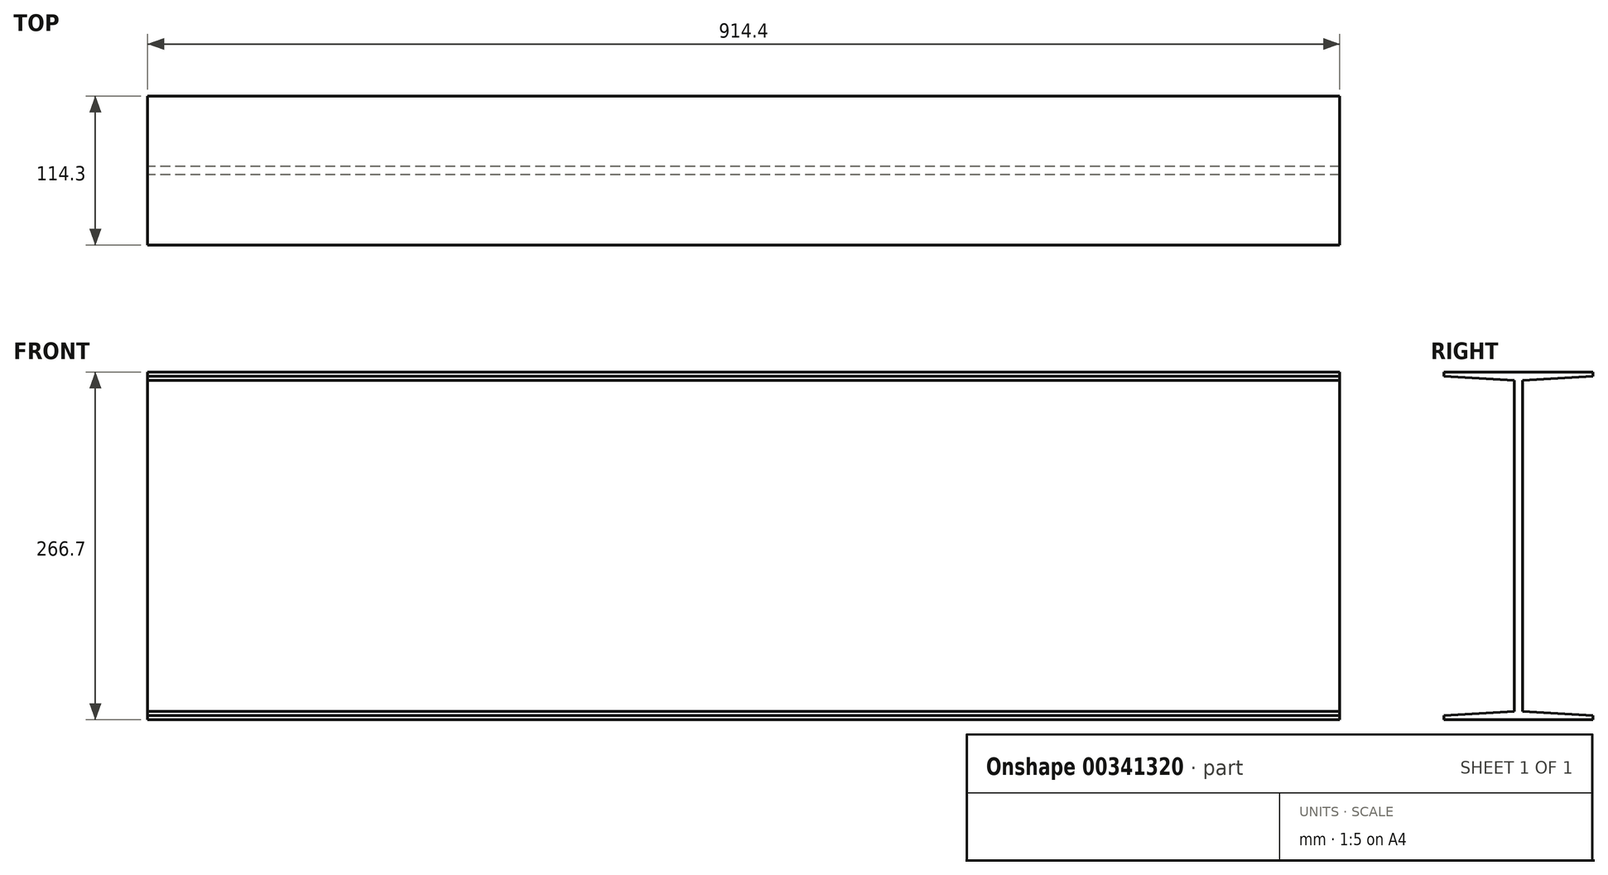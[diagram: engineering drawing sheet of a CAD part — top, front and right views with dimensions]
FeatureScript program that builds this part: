
annotation { "Feature Type Name" : "Feature", "Feature Type Description" : "" }
export const myFeature = defineFeature(function(context is Context, id is Id, definition is map)
    precondition{}
    {
        {
            var Q0;
            Q0=qCreatedBy(makeId("Right.planeOp"),FACE);
            var sketch = newSketch(context, id + "F0", { "sketchPlane" : qUnion([Q0])});
            skLineSegment(sketch, "E0.bottom", {"start": v(57.15, 133.35) * mm, "end": v(-57.15, 133.35) * mm});
            skLineSegment(sketch, "E0.top", {"start": v(57.15, -133.35) * mm, "end": v(-57.15, -133.35) * mm});
            skLineSegment(sketch, "E0.left", {"start": v(57.15, 133.35) * mm, "end": v(57.15, 130.18) * mm});
            skLineSegment(sketch, "E0.right", {"start": v(-57.15, 133.35) * mm, "end": v(-57.15, 130.18) * mm});
            skPoint(sketch, "E0.middle", {"position": v(0, 0) * mm});
            skLineSegment(sketch, "E1.left", {"start": v(3.18, 127) * mm, "end": v(3.17, -127) * mm});
            skLineSegment(sketch, "E1.right", {"start": v(-3.18, 127) * mm, "end": v(-3.18, -127) * mm});
            skLineSegment(sketch, "E2.trimOffspring", {"start": v(-57.15, -130.17) * mm, "end": v(-57.15, -133.35) * mm});
            skLineSegment(sketch, "E3.trimOffspring", {"start": v(57.15, -130.17) * mm, "end": v(57.15, -133.35) * mm});
            skLineSegment(sketch, "E4", {"start": v(-57.15, 130.18) * mm, "end": v(-3.17, 127) * mm});
            skLineSegment(sketch, "E5", {"start": v(3.17, 127) * mm, "end": v(57.15, 130.18) * mm});
            skLineSegment(sketch, "E6", {"start": v(-57.15, -130.17) * mm, "end": v(-3.18, -127) * mm});
            skLineSegment(sketch, "E7", {"start": v(3.17, -127) * mm, "end": v(57.15, -130.17) * mm});
            skSolve(sketch);
        }
        {
            var Q0;
            Q0 = qSketchRegion(id + "F0", true);
            extrude(context, id + "F1", {"entities" : qUnion([Q0]), "depth" : 914.4 * mm});
        }
    });
